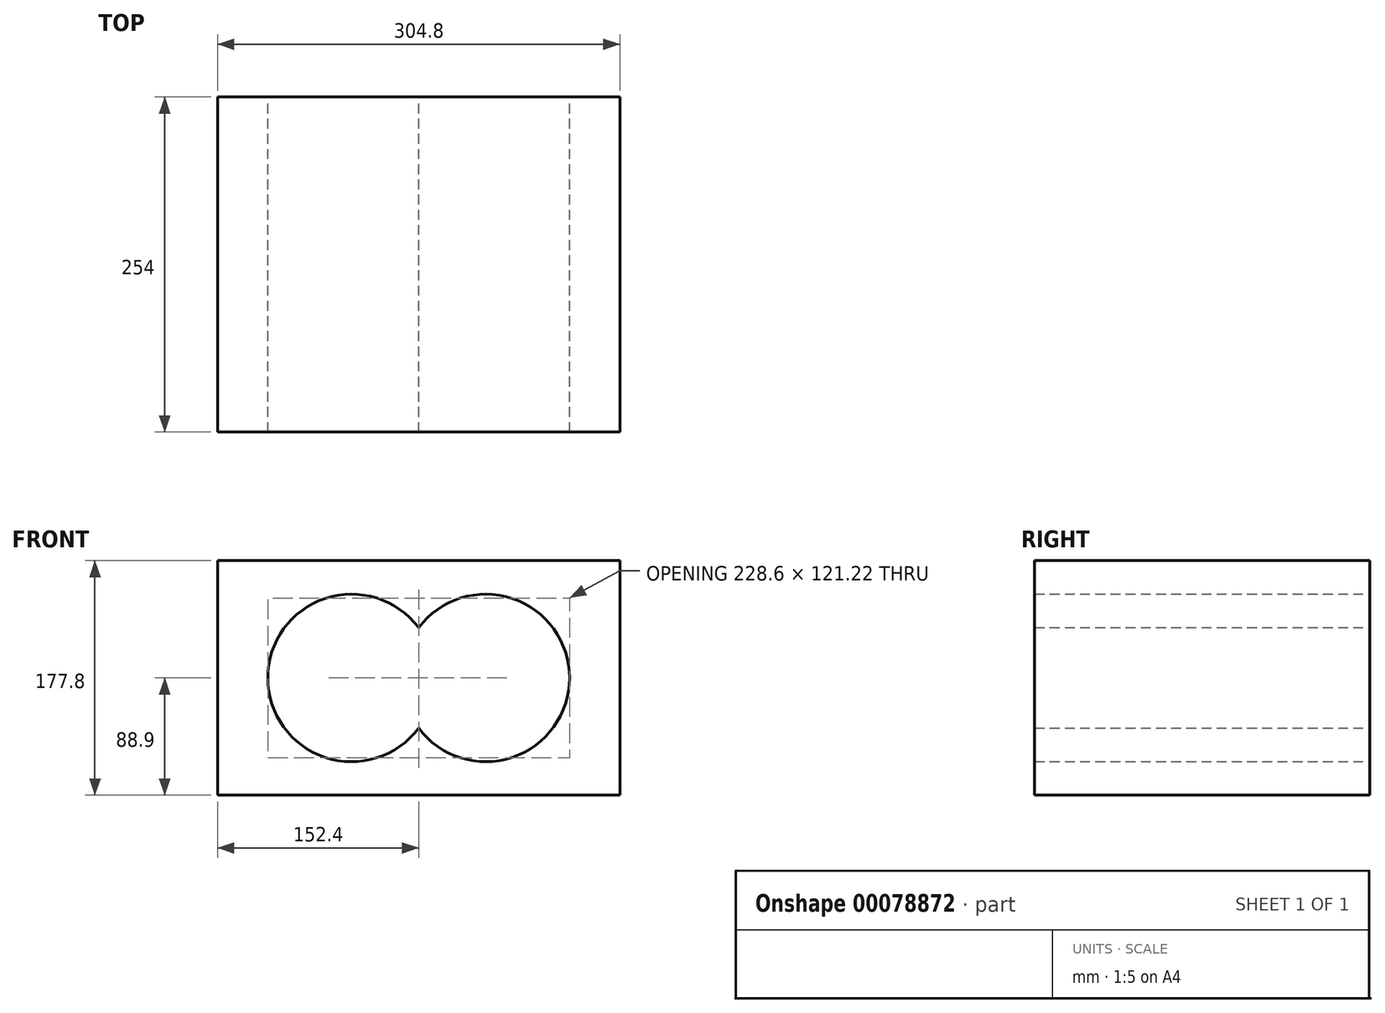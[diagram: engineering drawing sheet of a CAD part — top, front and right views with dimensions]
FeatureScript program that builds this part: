
annotation { "Feature Type Name" : "Feature", "Feature Type Description" : "" }
export const myFeature = defineFeature(function(context is Context, id is Id, definition is map)
    precondition{}
    {
        {
            var Q0;
            Q0=qCreatedBy(makeId("Front.planeOp"),FACE);
            var sketch = newSketch(context, id + "F0", { "sketchPlane" : qUnion([Q0])});
            skLineSegment(sketch, "E0.bottom", {"start": v(0, 0) * mm, "end": v(304.8, 0) * mm});
            skLineSegment(sketch, "E0.top", {"start": v(0, 177.8) * mm, "end": v(304.8, 177.8) * mm});
            skLineSegment(sketch, "E0.left", {"start": v(0, 0) * mm, "end": v(0, 177.8) * mm});
            skLineSegment(sketch, "E0.right", {"start": v(304.8, 0) * mm, "end": v(304.8, 177.8) * mm});
            skCircle(sketch, "E1", {"center": v(101.6, 88.9) * mm, "radius": 63.5 * mm});
            skPoint(sketch, "E1.centerSnap0", {"position": v(0, 88.9) * mm});
            skCircle(sketch, "E2", {"center": v(203.2, 88.9) * mm, "radius": 63.5 * mm});
            skLineSegment(sketch, "E3", {"start": v(101.6, 88.9) * mm, "end": v(203.2, 88.9) * mm, "construction": true});
            skPoint(sketch, "E4", {"position": v(152.4, 88.9) * mm});
            skPoint(sketch, "E5", {"position": v(152.4, 0) * mm});
            skLineSegment(sketch, "E6", {"start": v(152.4, 0) * mm, "end": v(152.4, 177.8) * mm, "construction": true});
            skSolve(sketch);
        }
        {
            var Q0;
            Q0=makeQuery(id+"F0.imprint","IMPRINT",FACE,{"disambiguationData":[TD([[makeQuery(id+"F0.imprint","IMPRINT",EDGE,{"derivedFrom":sQuery(id+"F0.wireOp",EDGE,"E0.bottom")}),1.0]])]});
            extrude(context, id + "F1", {"entities" : qUnion([Q0]), "depth" : 254 * mm});
        }
    });
